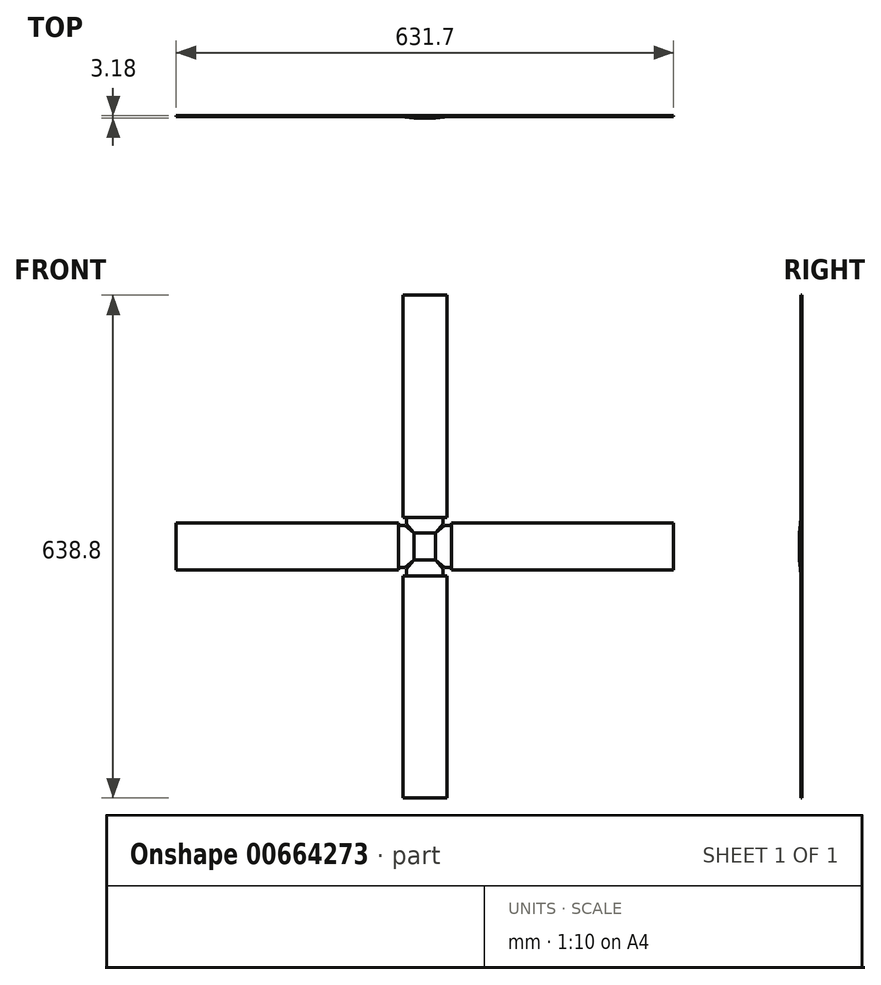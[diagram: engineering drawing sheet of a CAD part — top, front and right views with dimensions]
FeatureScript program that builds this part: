
annotation { "Feature Type Name" : "Feature", "Feature Type Description" : "" }
export const myFeature = defineFeature(function(context is Context, id is Id, definition is map)
    precondition{}
    {
        {
            var Q0;
            Q0=qCreatedBy(makeId("Front.planeOp"),FACE);
            var sketch = newSketch(context, id + "F0", { "sketchPlane" : qUnion([Q0])});
            skLineSegment(sketch, "E0.bottom", {"start": v(13.72, -17.27) * mm, "end": v(-13.72, -17.27) * mm});
            skLineSegment(sketch, "E0.top", {"start": v(13.72, 17.27) * mm, "end": v(-13.72, 17.27) * mm});
            skLineSegment(sketch, "E0.left", {"start": v(13.72, -17.27) * mm, "end": v(13.72, 17.27) * mm});
            skLineSegment(sketch, "E0.right", {"start": v(-13.72, -17.27) * mm, "end": v(-13.72, 17.27) * mm});
            skPoint(sketch, "E0.middle", {"position": v(0, 0) * mm});
            skLineSegment(sketch, "E1", {"start": v(0, 0) * mm, "end": v(200.92, 0) * mm, "construction": true});
            skLineSegment(sketch, "E2.bottom", {"start": v(33.66, -29.97) * mm, "end": v(315.85, -29.97) * mm});
            skLineSegment(sketch, "E2.top", {"start": v(33.66, 29.97) * mm, "end": v(315.85, 29.97) * mm});
            skLineSegment(sketch, "E2.left", {"start": v(33.66, -29.97) * mm, "end": v(33.66, 29.97) * mm});
            skLineSegment(sketch, "E2.right", {"start": v(315.85, -29.97) * mm, "end": v(315.85, 29.97) * mm});
            skLineSegment(sketch, "E3", {"start": v(33.66, 26.8) * mm, "end": v(25.07, 26.8) * mm});
            skLineSegment(sketch, "E4", {"start": v(25.07, 26.8) * mm, "end": v(13.72, 17.27) * mm});
            skLineSegment(sketch, "E5", {"start": v(33.66, -26.8) * mm, "end": v(25.07, -26.8) * mm});
            skLineSegment(sketch, "E6", {"start": v(25.07, -26.8) * mm, "end": v(13.72, -17.27) * mm});
            skLineSegment(sketch, "E7", {"start": v(0, 0) * mm, "end": v(0, 94.18) * mm, "construction": true});
            skLineSegment(sketch, "E8.bottom", {"start": v(-27.94, 37.21) * mm, "end": v(27.94, 37.21) * mm});
            skLineSegment(sketch, "E8.top", {"start": v(-27.94, 319.4) * mm, "end": v(27.94, 319.4) * mm});
            skLineSegment(sketch, "E8.left", {"start": v(-27.94, 37.21) * mm, "end": v(-27.94, 319.4) * mm});
            skLineSegment(sketch, "E8.right", {"start": v(27.94, 37.21) * mm, "end": v(27.94, 319.4) * mm});
            skLineSegment(sketch, "E9", {"start": v(-23.24, 37.21) * mm, "end": v(-23.24, 28.62) * mm});
            skLineSegment(sketch, "E10", {"start": v(-23.24, 28.62) * mm, "end": v(-13.72, 17.27) * mm});
            skLineSegment(sketch, "E11", {"start": v(23.24, 37.21) * mm, "end": v(23.24, 28.62) * mm});
            skLineSegment(sketch, "E12", {"start": v(23.24, 28.62) * mm, "end": v(13.72, 17.27) * mm});
            skSolve(sketch);
        }
        {
            var Q0;
            Q0=makeQuery(id+"F0.imprint","IMPRINT",FACE,{"disambiguationData":[TD([[makeQuery(id+"F0.imprint","IMPRINT",EDGE,{"derivedFrom":sQuery(id+"F0.wireOp",EDGE,"E0.bottom")}),-1.0]])]});
            extrude(context, id + "F1", {"entities" : qUnion([Q0]), "depth" : 3.17 * mm, "offsetDistance" : 25.4 * mm});
        }
        {
            var Q0;
            {var subQ3=sQuery(id+"F0.wireOp",EDGE,"E2.bottom");Q0=makeQuery(id+"F0.imprint","IMPRINT",FACE,{"disambiguationData":[TD([[makeQuery(id+"F0.imprint","IMPRINT",EDGE,{"derivedFrom":subQ3}),1.0]])]});}
            extrude(context, id + "F2", {"entities" : qUnion([Q0]), "depth" : 1.52 * mm, "offsetDistance" : 25.4 * mm});
        }
        {
            var Q0;
            Q0=makeQuery(id+"F0.imprint","IMPRINT",FACE,{"disambiguationData":[TD([[makeQuery(id+"F0.imprint","IMPRINT",EDGE,{"derivedFrom":sQuery(id+"F0.wireOp",EDGE,"E8.top")}),-1.0]])]});
            extrude(context, id + "F3", {"entities" : qUnion([Q0]), "depth" : 1.52 * mm, "offsetDistance" : 25.4 * mm});
        }
        {
            var Q0;
            Q0=makeQuery(id+"F0.imprint","IMPRINT",FACE,{"disambiguationData":[TD([[makeQuery(id+"F0.imprint","IMPRINT",EDGE,{"derivedFrom":sQuery(id+"F0.wireOp",EDGE,"E0.top")}),-1.0]])]});
            extrude(context, id + "F4", {"entities" : qUnion([Q0]), "depth" : 3.17 * mm, "offsetDistance" : 25.4 * mm});
        }
        {
            var Q0;
            Q0=makeQuery(id+"F0.imprint","IMPRINT",FACE,{"disambiguationData":[TD([[makeQuery(id+"F0.imprint","IMPRINT",EDGE,{"derivedFrom":sQuery(id+"F0.wireOp",EDGE,"E0.left")}),-1.0]])]});
            extrude(context, id + "F5", {"entities" : qUnion([Q0]), "depth" : 3.17 * mm, "offsetDistance" : 25.4 * mm});
        }
        {
            var Q0;
            Q0=makeQuery(id+"F4.opExtrude","SWEPT_FACE",FACE,{"disambiguationData":[OSD([sQuery(id+"F0.wireOp",EDGE,"E9")])]});
            var sketch = newSketch(context, id + "F6", { "sketchPlane" : qUnion([Q0])});
            skLineSegment(sketch, "E13.0", {"start": v(0, 37.21) * mm, "end": v(0, 28.62) * mm});
            skLineSegment(sketch, "E14.0", {"start": v(0, 28.62) * mm, "end": v(0, 17.27) * mm});
            skLineSegment(sketch, "E15.0", {"start": v(3.18, 17.27) * mm, "end": v(0, 17.27) * mm});
            skLineSegment(sketch, "E16.0", {"start": v(1.52, 37.21) * mm, "end": v(0, 37.21) * mm});
            skLineSegment(sketch, "E17", {"start": v(1.52, 37.21) * mm, "end": v(3.17, 17.27) * mm});
            skSolve(sketch);
        }
        {
            var Q0;
            {var subQ0=sQuery(id+"F6.wireOp",EDGE,"E14.0");Q0=makeQuery(id+"F6.imprint","IMPRINT",FACE,{"disambiguationData":[TD([[makeQuery(id+"F6.imprint","IMPRINT",EDGE,{"derivedFrom":subQ0}),1.0]])]});}
            var Q1;
            {var subQ0=sQuery(id+"F6.wireOp",EDGE,"E13.0");Q1=makeQuery(id+"F6.imprint","IMPRINT",FACE,{"disambiguationData":[TD([[makeQuery(id+"F6.imprint","IMPRINT",EDGE,{"derivedFrom":subQ0}),1.0]])]});}
            extrude(context, id + "F7", {"entities" : qUnion([Q0, Q1]), "oppositeDirection" : true, "depth" : 50.8 * mm, "offsetDistance" : 25.4 * mm});
        }
        {
            var Q0;
            Q0=makeQuery(id+"F7.opExtrude","SWEPT_BODY",BODY,{"disambiguationData":[OSD([sQuery(id+"F6.wireOp",EDGE,"E13.0"),sQuery(id+"F6.wireOp",EDGE,"E14.0"),sQuery(id+"F6.wireOp",EDGE,"E15.0"),sQuery(id+"F6.wireOp",EDGE,"E16.0"),sQuery(id+"F6.wireOp",EDGE,"E17")])]});
            var Q1;
            Q1=makeQuery(id+"F4.opExtrude","SWEPT_BODY",BODY,{"disambiguationData":[OSD([sQuery(id+"F0.wireOp",EDGE,"E0.top"),sQuery(id+"F0.wireOp",EDGE,"E8.bottom"),sQuery(id+"F0.wireOp",EDGE,"E9"),sQuery(id+"F0.wireOp",EDGE,"E10"),sQuery(id+"F0.wireOp",EDGE,"E11"),sQuery(id+"F0.wireOp",EDGE,"E12")])]});
            booleanBodies(context, id + "F8", {"operationType" : BooleanOperationType.INTERSECTION, "tools" : qUnion([Q0, Q1])});
        }
        {
            var Q0;
            Q0=makeQuery(id+"F5.opExtrude","SWEPT_FACE",FACE,{"disambiguationData":[OSD([sQuery(id+"F0.wireOp",EDGE,"E5")])]});
            var sketch = newSketch(context, id + "F9", { "sketchPlane" : qUnion([Q0])});
            skLineSegment(sketch, "E18.0", {"start": v(25.07, 0) * mm, "end": v(13.72, 0) * mm});
            skLineSegment(sketch, "E19.0", {"start": v(33.66, 0) * mm, "end": v(25.07, 0) * mm});
            skLineSegment(sketch, "E20.0", {"start": v(13.72, 3.18) * mm, "end": v(13.72, 0) * mm});
            skLineSegment(sketch, "E21.0", {"start": v(33.66, 1.52) * mm, "end": v(33.66, 0) * mm});
            skLineSegment(sketch, "E22", {"start": v(13.72, 3.18) * mm, "end": v(33.66, 1.52) * mm});
            skSolve(sketch);
        }
        {
            var Q0;
            {var subQ0=sQuery(id+"F9.wireOp",EDGE,"E18.0");Q0=makeQuery(id+"F9.imprint","IMPRINT",FACE,{"disambiguationData":[TD([[makeQuery(id+"F9.imprint","IMPRINT",EDGE,{"derivedFrom":subQ0}),-1.0]])]});}
            var Q1;
            {var subQ0=sQuery(id+"F9.wireOp",EDGE,"E19.0");Q1=makeQuery(id+"F9.imprint","IMPRINT",FACE,{"disambiguationData":[TD([[makeQuery(id+"F9.imprint","IMPRINT",EDGE,{"derivedFrom":subQ0}),-1.0]])]});}
            extrude(context, id + "F10", {"entities" : qUnion([Q0, Q1]), "oppositeDirection" : true, "depth" : 63.5 * mm, "offsetDistance" : 25.4 * mm});
        }
        {
            var Q0;
            Q0=makeQuery(id+"F10.opExtrude","SWEPT_BODY",BODY,{"disambiguationData":[OSD([sQuery(id+"F9.wireOp",EDGE,"E18.0"),sQuery(id+"F9.wireOp",EDGE,"E19.0"),sQuery(id+"F9.wireOp",EDGE,"E20.0"),sQuery(id+"F9.wireOp",EDGE,"E21.0"),sQuery(id+"F9.wireOp",EDGE,"E22")])]});
            var Q1;
            Q1=makeQuery(id+"F5.opExtrude","SWEPT_BODY",BODY,{"disambiguationData":[OSD([sQuery(id+"F0.wireOp",EDGE,"E0.left"),sQuery(id+"F0.wireOp",EDGE,"E2.left"),sQuery(id+"F0.wireOp",EDGE,"E3"),sQuery(id+"F0.wireOp",EDGE,"E4"),sQuery(id+"F0.wireOp",EDGE,"E5"),sQuery(id+"F0.wireOp",EDGE,"E6")])]});
            booleanBodies(context, id + "F11", {"operationType" : BooleanOperationType.INTERSECTION, "tools" : qUnion([Q0, Q1])});
        }
        {
            var Q0;
            Q0=makeQuery(id+"F2.opExtrude","SWEPT_BODY",BODY,{"disambiguationData":[OSD([sQuery(id+"F0.wireOp",EDGE,"E2.bottom"),sQuery(id+"F0.wireOp",EDGE,"E2.top"),sQuery(id+"F0.wireOp",EDGE,"E2.left"),sQuery(id+"F0.wireOp",EDGE,"E2.right")])]});
            var Q1;
            Q1=makeQuery(id+"F11.opBoolean","INTERSECT",BODY,{"derivedFrom":[makeQuery(id+"F5.opExtrude","SWEPT_BODY",BODY,{"disambiguationData":[OSD([sQuery(id+"F0.wireOp",EDGE,"E0.left"),sQuery(id+"F0.wireOp",EDGE,"E2.left"),sQuery(id+"F0.wireOp",EDGE,"E3"),sQuery(id+"F0.wireOp",EDGE,"E4"),sQuery(id+"F0.wireOp",EDGE,"E5"),sQuery(id+"F0.wireOp",EDGE,"E6")])]}),makeQuery(id+"F10.opExtrude","SWEPT_BODY",BODY,{"disambiguationData":[OSD([sQuery(id+"F9.wireOp",EDGE,"E18.0"),sQuery(id+"F9.wireOp",EDGE,"E19.0"),sQuery(id+"F9.wireOp",EDGE,"E20.0"),sQuery(id+"F9.wireOp",EDGE,"E21.0"),sQuery(id+"F9.wireOp",EDGE,"E22")])]})]});
            var Q2;
            Q2=qCreatedBy(makeId("Right.planeOp"),FACE);
            mirror(context, id + "F12", {"entities" : qUnion([Q0, Q1]), "mirrorPlane" : qUnion([Q2])});
        }
        {
            var Q0;
            Q0=makeQuery(id+"F3.opExtrude","SWEPT_BODY",BODY,{"disambiguationData":[OSD([sQuery(id+"F0.wireOp",EDGE,"E8.bottom"),sQuery(id+"F0.wireOp",EDGE,"E8.top"),sQuery(id+"F0.wireOp",EDGE,"E8.left"),sQuery(id+"F0.wireOp",EDGE,"E8.right")])]});
            var Q1;
            Q1=makeQuery(id+"F8.opBoolean","INTERSECT",BODY,{"derivedFrom":[makeQuery(id+"F4.opExtrude","SWEPT_BODY",BODY,{"disambiguationData":[OSD([sQuery(id+"F0.wireOp",EDGE,"E0.top"),sQuery(id+"F0.wireOp",EDGE,"E8.bottom"),sQuery(id+"F0.wireOp",EDGE,"E9"),sQuery(id+"F0.wireOp",EDGE,"E10"),sQuery(id+"F0.wireOp",EDGE,"E11"),sQuery(id+"F0.wireOp",EDGE,"E12")])]}),makeQuery(id+"F7.opExtrude","SWEPT_BODY",BODY,{"disambiguationData":[OSD([sQuery(id+"F6.wireOp",EDGE,"E13.0"),sQuery(id+"F6.wireOp",EDGE,"E14.0"),sQuery(id+"F6.wireOp",EDGE,"E15.0"),sQuery(id+"F6.wireOp",EDGE,"E16.0"),sQuery(id+"F6.wireOp",EDGE,"E17")])]})]});
            var Q2;
            Q2=qCreatedBy(makeId("Top.planeOp"),FACE);
            mirror(context, id + "F13", {"entities" : qUnion([Q0, Q1]), "mirrorPlane" : qUnion([Q2])});
        }
    });
